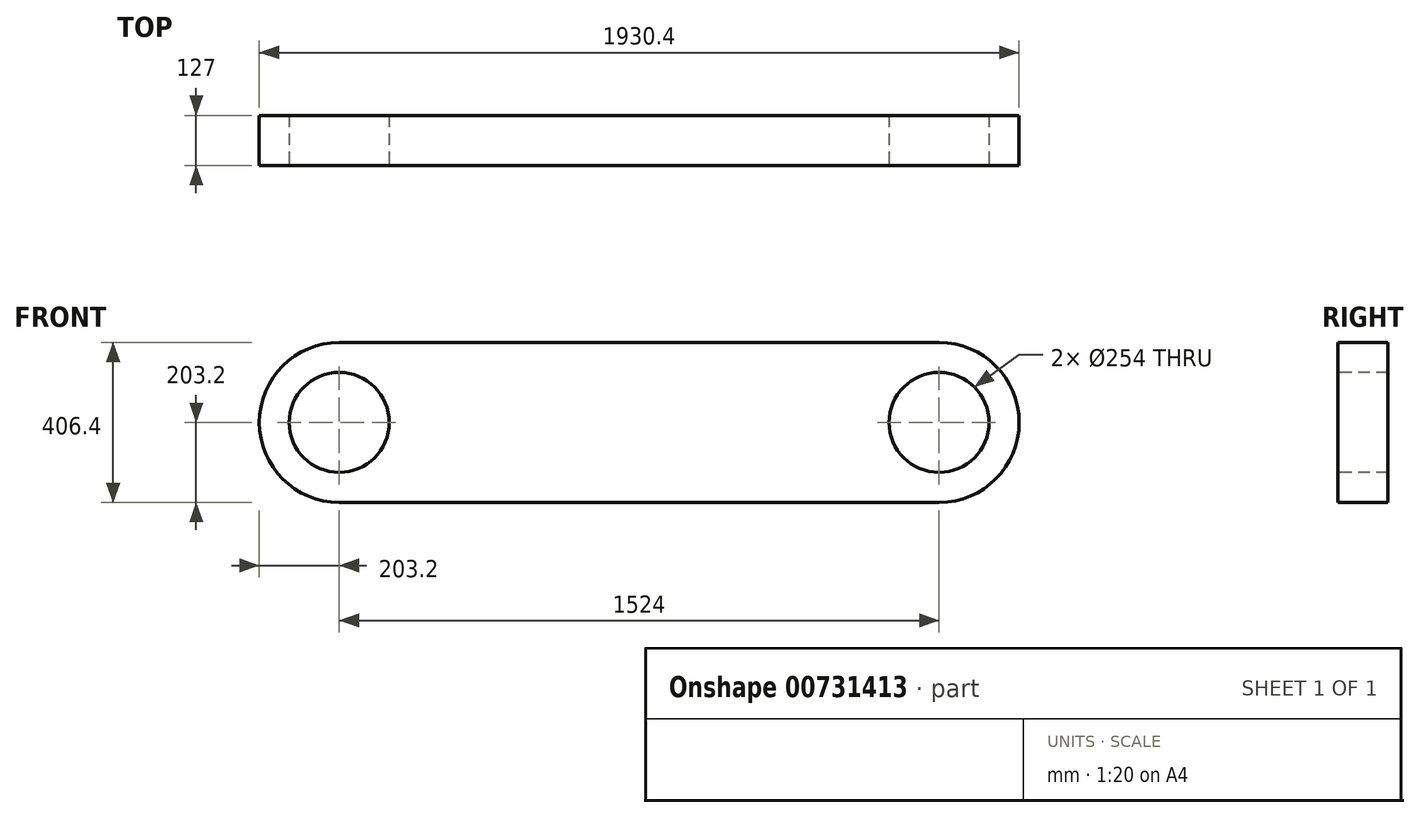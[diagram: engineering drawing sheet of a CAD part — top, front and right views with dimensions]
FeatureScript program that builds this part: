
annotation { "Feature Type Name" : "Feature", "Feature Type Description" : "" }
export const myFeature = defineFeature(function(context is Context, id is Id, definition is map)
    precondition{}
    {
        {
            var Q0;
            Q0=qCreatedBy(makeId("Front.planeOp"),FACE);
            var sketch = newSketch(context, id + "F0", { "sketchPlane" : qUnion([Q0])});
            skLineSegment(sketch, "E0.bottom", {"start": v(-762, 203.2) * mm, "end": v(762, 203.2) * mm});
            skLineSegment(sketch, "E0.top", {"start": v(-762, -203.2) * mm, "end": v(762, -203.2) * mm});
            skArc(sketch, "E1", {"start": v(762, -203.2) * mm, "mid": v(965.2, 0) * mm, "end": v(762, 203.2) * mm});
            skArc(sketch, "E2", {"start": v(-762, 203.2) * mm, "mid": v(-965.2, 0) * mm, "end": v(-762, -203.2) * mm});
            skSolve(sketch);
        }
        {
            var Q0;
            Q0 = qSketchRegion(id + "F0", true);
            extrude(context, id + "F1", {"entities" : qUnion([Q0]), "depth" : 127 * mm, "offsetDistance" : 25.4 * mm});
        }
        {
            var Q0;
            Q0=makeQuery(id+"F1.opExtrude","CAP_FACE",FACE,{"disambiguationData":[OSD([sQuery(id+"F0.wireOp",EDGE,"E0.bottom"),sQuery(id+"F0.wireOp",EDGE,"E0.top"),sQuery(id+"F0.wireOp",EDGE,"E1"),sQuery(id+"F0.wireOp",EDGE,"E2")])],"isStart":false});
            var sketch = newSketch(context, id + "F2", { "sketchPlane" : qUnion([Q0])});
            skCircle(sketch, "E3", {"center": v(762, 0) * mm, "radius": 127 * mm});
            skCircle(sketch, "E4", {"center": v(-762, 0) * mm, "radius": 127 * mm});
            skSolve(sketch);
        }
        {
            var Q0;
            Q0=makeQuery(id+"F2.imprint","IMPRINT",FACE,{"disambiguationData":[TD([[makeQuery(id+"F2.imprint","IMPRINT",EDGE,{"derivedFrom":sQuery(id+"F2.wireOp",EDGE,"E4")}),1.0]])]});
            var Q1;
            Q1=makeQuery(id+"F2.imprint","IMPRINT",FACE,{"disambiguationData":[TD([[makeQuery(id+"F2.imprint","IMPRINT",EDGE,{"derivedFrom":sQuery(id+"F2.wireOp",EDGE,"E3")}),1.0]])]});
            extrude(context, id + "F3", {"entities" : qUnion([Q0, Q1]), "operationType" : NewBodyOperationType.REMOVE, "oppositeDirection" : true, "depth" : 1226.82 * mm, "offsetDistance" : 25.4 * mm});
        }
    });
